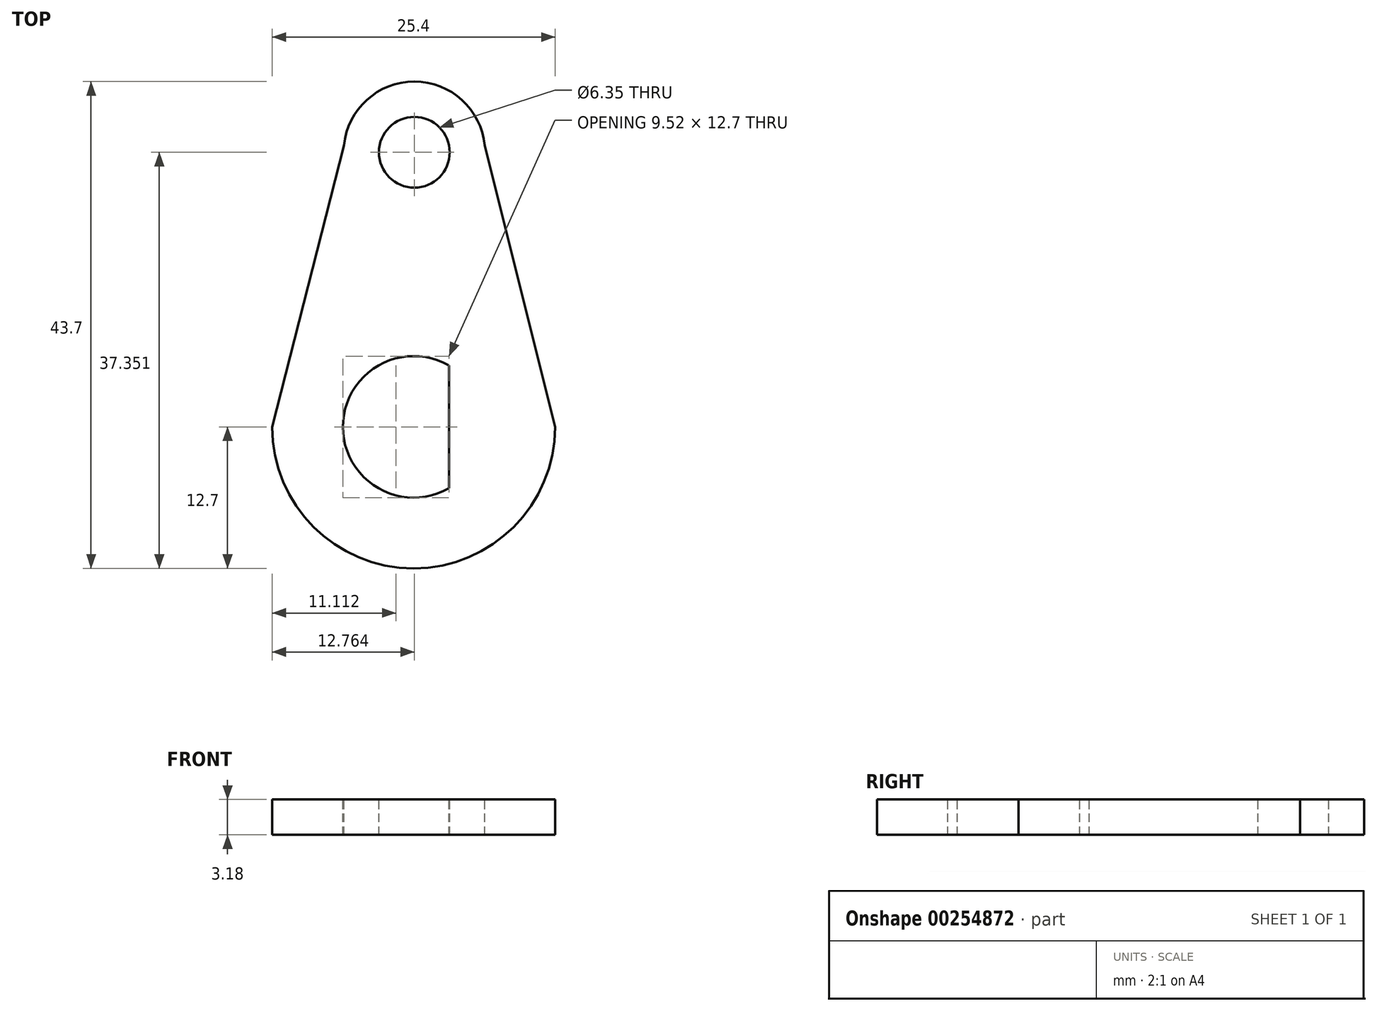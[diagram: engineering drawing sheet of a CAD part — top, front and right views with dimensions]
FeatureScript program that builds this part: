
annotation { "Feature Type Name" : "Feature", "Feature Type Description" : "" }
export const myFeature = defineFeature(function(context is Context, id is Id, definition is map)
    precondition{}
    {
        {
            var Q0;
            Q0=qCreatedBy(makeId("Top.planeOp"),FACE);
            var sketch = newSketch(context, id + "F0", { "sketchPlane" : qUnion([Q0])});
            skArc(sketch, "E0", {"start": v(-12.7, 0) * mm, "mid": v(0, -12.7) * mm, "end": v(12.7, 0) * mm});
            skCircle(sketch, "E1", {"center": v(0.06, 24.65) * mm, "radius": 3.18 * mm});
            skArc(sketch, "E2", {"start": v(6.39, 25.26) * mm, "mid": v(0.07, 31) * mm, "end": v(-6.26, 25.27) * mm});
            skLineSegment(sketch, "E3", {"start": v(12.7, 0) * mm, "end": v(6.39, 25.26) * mm});
            skArc(sketch, "E4", {"start": v(3.18, 5.5) * mm, "mid": v(-6.35, 0) * mm, "end": v(3.18, -5.5) * mm});
            skLineSegment(sketch, "E5", {"start": v(-12.7, 0) * mm, "end": v(-6.26, 25.27) * mm});
            skLineSegment(sketch, "E6.0", {"start": v(3.18, 5.5) * mm, "end": v(3.18, -5.5) * mm});
            skSolve(sketch);
        }
        {
            var Q0;
            Q0=makeQuery(id+"F0.imprint","IMPRINT",FACE,{"disambiguationData":[TD([[makeQuery(id+"F0.imprint","IMPRINT",EDGE,{"derivedFrom":sQuery(id+"F0.wireOp",EDGE,"E0")}),1.0]])]});
            extrude(context, id + "F1", {"entities" : qUnion([Q0]), "oppositeDirection" : true, "depth" : 3.17 * mm});
        }
    });
